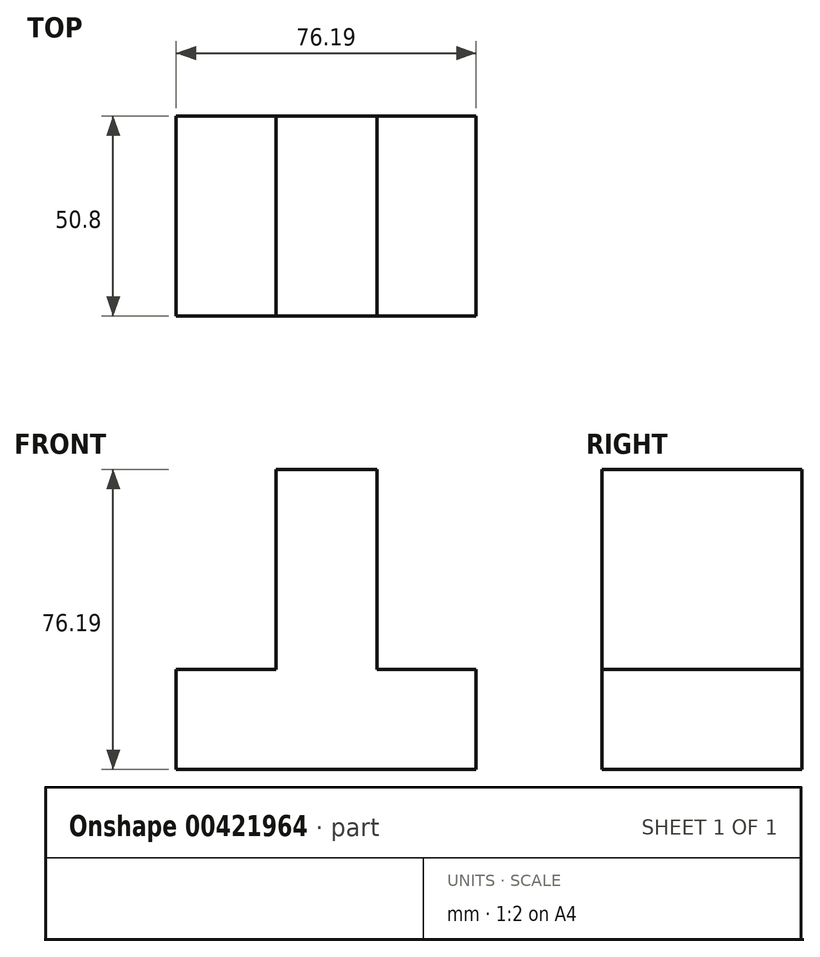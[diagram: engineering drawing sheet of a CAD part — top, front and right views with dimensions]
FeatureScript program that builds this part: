
annotation { "Feature Type Name" : "Feature", "Feature Type Description" : "" }
export const myFeature = defineFeature(function(context is Context, id is Id, definition is map)
    precondition{}
    {
        {
            var Q0;
            Q0=qCreatedBy(makeId("Front.planeOp"),FACE);
            var sketch = newSketch(context, id + "F0", { "sketchPlane" : qUnion([Q0])});
            skLineSegment(sketch, "E0", {"start": v(0, 0) * mm, "end": v(-76.2, 0) * mm});
            skLineSegment(sketch, "E1", {"start": v(-76.2, 0) * mm, "end": v(-76.2, 25.4) * mm});
            skLineSegment(sketch, "E2", {"start": v(-76.2, 25.4) * mm, "end": v(-50.8, 25.4) * mm});
            skLineSegment(sketch, "E3", {"start": v(-50.8, 25.4) * mm, "end": v(-50.8, 76.2) * mm});
            skLineSegment(sketch, "E4", {"start": v(-50.8, 76.2) * mm, "end": v(-25.23, 76.2) * mm});
            skLineSegment(sketch, "E5", {"start": v(-25.23, 76.2) * mm, "end": v(-25.23, 27.99) * mm});
            skLineSegment(sketch, "E6", {"start": v(-25.23, 27.99) * mm, "end": v(-25.23, 25.4) * mm});
            skLineSegment(sketch, "E7", {"start": v(-25.23, 25.4) * mm, "end": v(0, 25.4) * mm});
            skLineSegment(sketch, "E8", {"start": v(0, 25.4) * mm, "end": v(0, 0) * mm});
            skSolve(sketch);
        }
        {
            var Q0;
            Q0=makeQuery(id+"F0.imprint","IMPRINT",FACE,{"disambiguationData":[TD([[makeQuery(id+"F0.imprint","IMPRINT",EDGE,{"derivedFrom":sQuery(id+"F0.wireOp",EDGE,"E0")}),-1.0]])]});
            extrude(context, id + "F1", {"entities" : qUnion([Q0]), "depth" : 50.8 * mm});
        }
    });
